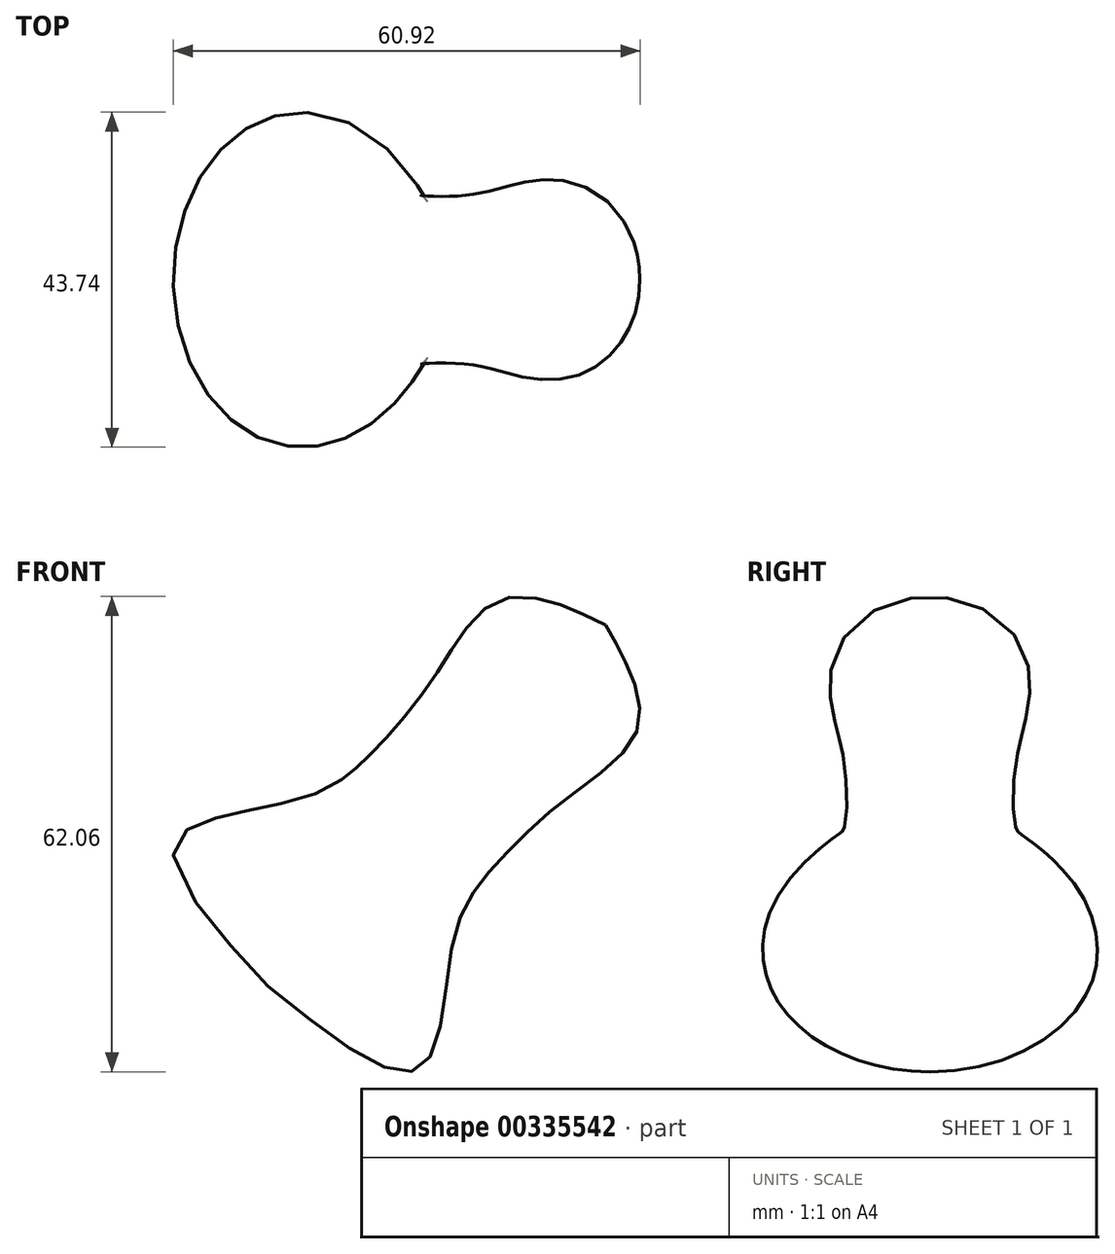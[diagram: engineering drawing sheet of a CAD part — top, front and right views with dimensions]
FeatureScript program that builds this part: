
annotation { "Feature Type Name" : "Feature", "Feature Type Description" : "" }
export const myFeature = defineFeature(function(context is Context, id is Id, definition is map)
    precondition{}
    {
        {
            var Q0;
            Q0=qCreatedBy(makeId("Front.planeOp"),FACE);
            var sketch = newSketch(context, id + "F0", { "sketchPlane" : qUnion([Q0])});
            skLineSegment(sketch, "E0", {"start": v(30.8, 36.84) * mm, "end": v(-13.24, -10.36) * mm});
            skFitSpline(sketch, "E1", {"points": [v(30.8, 36.84) * mm, v(33.96, 30.8) * mm, v(34.82, 22.74) * mm, v(25.61, 14.1) * mm, v(16.4, 5.47) * mm, v(10.94, -4.32) * mm, v(6.62, -21) * mm, v(-13.24, -10.36) * mm], "startDerivative": vector(31.5, -53.52) * mm, "endDerivative": vector(-126.97, 102.2) * mm});
            skSolve(sketch);
        }
        {
            var Q0;
            Q0=makeQuery(id+"F0.imprint","IMPRINT",FACE,{"disambiguationData":[TD([[makeQuery(id+"F0.imprint","IMPRINT",EDGE,{"derivedFrom":sQuery(id+"F0.wireOp",EDGE,"E0")}),1.0]])]});
            var Q1;
            Q1=sQuery(id+"F0.wireOp",EDGE,"E0");
            revolve(context, id + "F1", {"entities" : qUnion([Q0]), "axis" : qUnion([Q1]), "revolveType" : RevolveType.FULL});
        }
    });
